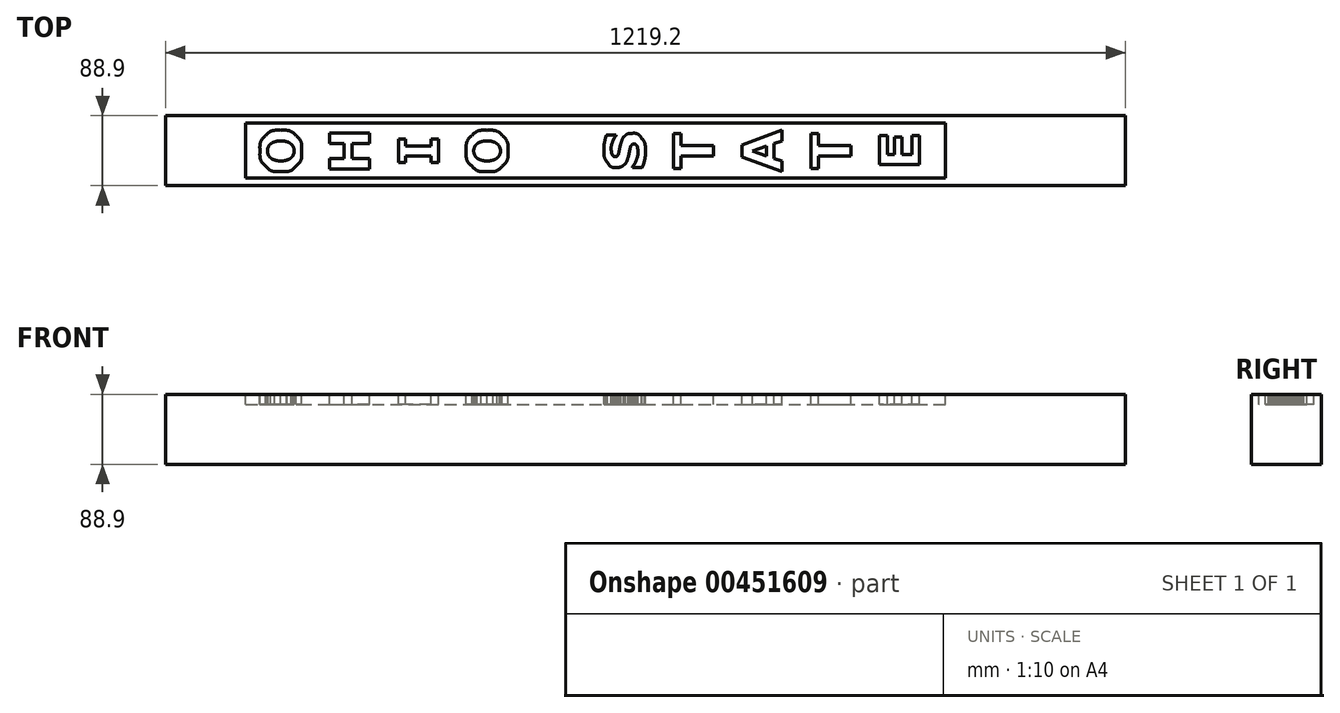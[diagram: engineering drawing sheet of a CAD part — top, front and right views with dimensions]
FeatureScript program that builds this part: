
annotation { "Feature Type Name" : "Feature", "Feature Type Description" : "" }
export const myFeature = defineFeature(function(context is Context, id is Id, definition is map)
    precondition{}
    {
        {
            var Q0;
            Q0=qCreatedBy(makeId("Right.planeOp"),FACE);
            var sketch = newSketch(context, id + "F0", { "sketchPlane" : qUnion([Q0])});
            skLineSegment(sketch, "E0.bottom", {"start": v(0, 0) * mm, "end": v(88.9, 0) * mm});
            skLineSegment(sketch, "E0.top", {"start": v(0, 88.9) * mm, "end": v(88.9, 88.9) * mm});
            skLineSegment(sketch, "E0.left", {"start": v(0, 0) * mm, "end": v(0, 88.9) * mm});
            skLineSegment(sketch, "E0.right", {"start": v(88.9, 0) * mm, "end": v(88.9, 88.9) * mm});
            skSolve(sketch);
        }
        {
            var Q0;
            Q0 = qSketchRegion(id + "F0", true);
            extrude(context, id + "F1", {"entities" : qUnion([Q0]), "depth" : 1219.2 * mm});
        }
        {
            var Q0;
            Q0=makeQuery(id+"F1.opExtrude","SWEPT_FACE",FACE,{"disambiguationData":[OSD([sQuery(id+"F0.wireOp",EDGE,"E0.top")])]});
            var sketch = newSketch(context, id + "F2", { "sketchPlane" : qUnion([Q0])});
            skFitSpline(sketch, "E1", {"points": [v(146.34, 70.3) * mm, v(154.44, 70.3) * mm, v(160.88, 67.98) * mm, v(165.65, 63.34) * mm]});
            skFitSpline(sketch, "E2", {"points": [v(165.65, 63.34) * mm, v(170.4, 58.7) * mm, v(172.78, 52.29) * mm, v(172.78, 44.1) * mm]});
            skFitSpline(sketch, "E3", {"points": [v(172.78, 44.1) * mm, v(172.78, 35.93) * mm, v(170.4, 29.53) * mm, v(165.65, 24.9) * mm]});
            skFitSpline(sketch, "E4", {"points": [v(165.65, 24.9) * mm, v(160.88, 20.25) * mm, v(154.44, 17.93) * mm, v(146.34, 17.93) * mm]});
            skFitSpline(sketch, "E5", {"points": [v(146.34, 17.93) * mm, v(138.18, 17.93) * mm, v(131.73, 20.25) * mm, v(127, 24.9) * mm]});
            skFitSpline(sketch, "E6", {"points": [v(127, 24.9) * mm, v(122.25, 29.53) * mm, v(119.87, 35.93) * mm, v(119.87, 44.1) * mm]});
            skFitSpline(sketch, "E7", {"points": [v(119.87, 44.1) * mm, v(119.87, 52.24) * mm, v(122.25, 58.64) * mm, v(127, 63.3) * mm]});
            skFitSpline(sketch, "E8", {"points": [v(127, 63.3) * mm, v(131.73, 67.97) * mm, v(138.18, 70.3) * mm, v(146.34, 70.3) * mm]});
            skFitSpline(sketch, "E9", {"points": [v(159.2, 52.94) * mm, v(157.66, 54.2) * mm, v(155.84, 55.15) * mm, v(153.75, 55.77) * mm]});
            skFitSpline(sketch, "E10", {"points": [v(153.75, 55.77) * mm, v(151.63, 56.38) * mm, v(149.15, 56.69) * mm, v(146.31, 56.69) * mm]});
            skFitSpline(sketch, "E11", {"points": [v(146.31, 56.69) * mm, v(143.26, 56.69) * mm, v(140.67, 56.34) * mm, v(138.53, 55.63) * mm]});
            skFitSpline(sketch, "E12", {"points": [v(138.53, 55.63) * mm, v(136.4, 54.93) * mm, v(134.66, 54) * mm, v(133.35, 52.87) * mm]});
            skFitSpline(sketch, "E13", {"points": [v(133.35, 52.87) * mm, v(131.98, 51.7) * mm, v(131, 50.37) * mm, v(130.38, 48.84) * mm]});
            skFitSpline(sketch, "E14", {"points": [v(130.38, 48.84) * mm, v(129.76, 47.34) * mm, v(129.46, 45.77) * mm, v(129.46, 44.13) * mm]});
            skFitSpline(sketch, "E15", {"points": [v(129.46, 44.13) * mm, v(129.46, 42.47) * mm, v(129.75, 40.9) * mm, v(130.34, 39.43) * mm]});
            skFitSpline(sketch, "E16", {"points": [v(130.34, 39.43) * mm, v(130.93, 37.97) * mm, v(131.91, 36.63) * mm, v(133.28, 35.4) * mm]});
            skFitSpline(sketch, "E17", {"points": [v(133.28, 35.4) * mm, v(134.55, 34.26) * mm, v(136.31, 33.33) * mm, v(138.57, 32.6) * mm]});
            skFitSpline(sketch, "E18", {"points": [v(138.57, 32.6) * mm, v(140.8, 31.9) * mm, v(143.39, 31.54) * mm, v(146.34, 31.54) * mm]});
            skFitSpline(sketch, "E19", {"points": [v(146.34, 31.54) * mm, v(149.37, 31.54) * mm, v(151.95, 31.89) * mm, v(154.09, 32.57) * mm]});
            skFitSpline(sketch, "E20", {"points": [v(154.09, 32.57) * mm, v(156.2, 33.27) * mm, v(157.93, 34.2) * mm, v(159.27, 35.33) * mm]});
            skFitSpline(sketch, "E21", {"points": [v(159.27, 35.33) * mm, v(160.62, 36.47) * mm, v(161.6, 37.8) * mm, v(162.24, 39.32) * mm]});
            skFitSpline(sketch, "E22", {"points": [v(162.24, 39.32) * mm, v(162.88, 40.85) * mm, v(163.2, 42.45) * mm, v(163.2, 44.13) * mm]});
            skFitSpline(sketch, "E23", {"points": [v(163.2, 44.13) * mm, v(163.2, 45.82) * mm, v(162.88, 47.42) * mm, v(162.24, 48.94) * mm]});
            skFitSpline(sketch, "E24", {"points": [v(162.24, 48.94) * mm, v(161.58, 50.47) * mm, v(160.57, 51.8) * mm, v(159.2, 52.94) * mm]});
            skLineSegment(sketch, "E25", {"start": v(259.07, 66.86) * mm, "end": v(259.07, 53.75) * mm});
            skLineSegment(sketch, "E26", {"start": v(259.07, 53.75) * mm, "end": v(236.69, 53.75) * mm});
            skLineSegment(sketch, "E27", {"start": v(236.69, 53.75) * mm, "end": v(236.69, 34.41) * mm});
            skLineSegment(sketch, "E28", {"start": v(236.69, 34.41) * mm, "end": v(259.07, 34.41) * mm});
            skLineSegment(sketch, "E29", {"start": v(259.07, 34.41) * mm, "end": v(259.07, 21.3) * mm});
            skLineSegment(sketch, "E30", {"start": v(259.07, 21.3) * mm, "end": v(208.27, 21.3) * mm});
            skLineSegment(sketch, "E31", {"start": v(208.27, 21.3) * mm, "end": v(208.27, 34.41) * mm});
            skLineSegment(sketch, "E32", {"start": v(208.27, 34.41) * mm, "end": v(226.86, 34.41) * mm});
            skLineSegment(sketch, "E33", {"start": v(226.86, 34.41) * mm, "end": v(226.86, 53.75) * mm});
            skLineSegment(sketch, "E34", {"start": v(226.86, 53.75) * mm, "end": v(208.27, 53.75) * mm});
            skLineSegment(sketch, "E35", {"start": v(208.27, 53.75) * mm, "end": v(208.27, 66.86) * mm});
            skLineSegment(sketch, "E36", {"start": v(208.27, 66.86) * mm, "end": v(259.07, 66.86) * mm});
            skFitSpline(sketch, "E37", {"points": [v(408.36, 70.3) * mm, v(416.46, 70.3) * mm, v(422.9, 67.98) * mm, v(427.67, 63.34) * mm]});
            skFitSpline(sketch, "E38", {"points": [v(427.67, 63.34) * mm, v(432.43, 58.7) * mm, v(434.8, 52.29) * mm, v(434.8, 44.1) * mm]});
            skFitSpline(sketch, "E39", {"points": [v(434.8, 44.1) * mm, v(434.8, 35.93) * mm, v(432.43, 29.53) * mm, v(427.67, 24.9) * mm]});
            skFitSpline(sketch, "E40", {"points": [v(427.67, 24.9) * mm, v(422.9, 20.25) * mm, v(416.46, 17.93) * mm, v(408.36, 17.93) * mm]});
            skFitSpline(sketch, "E41", {"points": [v(408.36, 17.93) * mm, v(400.2, 17.93) * mm, v(393.75, 20.25) * mm, v(389.02, 24.9) * mm]});
            skFitSpline(sketch, "E42", {"points": [v(389.02, 24.9) * mm, v(384.26, 29.53) * mm, v(381.89, 35.93) * mm, v(381.89, 44.1) * mm]});
            skFitSpline(sketch, "E43", {"points": [v(381.89, 44.1) * mm, v(381.89, 52.24) * mm, v(384.26, 58.64) * mm, v(389.02, 63.3) * mm]});
            skFitSpline(sketch, "E44", {"points": [v(389.02, 63.3) * mm, v(393.75, 67.97) * mm, v(400.2, 70.3) * mm, v(408.36, 70.3) * mm]});
            skLineSegment(sketch, "E45", {"start": v(346.4, 58.94) * mm, "end": v(346.4, 29.2) * mm});
            skLineSegment(sketch, "E46", {"start": v(346.4, 29.2) * mm, "end": v(337.4, 29.2) * mm});
            skLineSegment(sketch, "E47", {"start": v(337.4, 29.2) * mm, "end": v(337.4, 37.52) * mm});
            skLineSegment(sketch, "E48", {"start": v(337.4, 37.52) * mm, "end": v(304.61, 37.52) * mm});
            skLineSegment(sketch, "E49", {"start": v(304.61, 37.52) * mm, "end": v(304.61, 29.2) * mm});
            skLineSegment(sketch, "E50", {"start": v(304.61, 29.2) * mm, "end": v(295.6, 29.2) * mm});
            skLineSegment(sketch, "E51", {"start": v(295.6, 29.2) * mm, "end": v(295.6, 58.94) * mm});
            skLineSegment(sketch, "E52", {"start": v(295.6, 58.94) * mm, "end": v(304.61, 58.94) * mm});
            skLineSegment(sketch, "E53", {"start": v(304.61, 58.94) * mm, "end": v(304.61, 50.62) * mm});
            skLineSegment(sketch, "E54", {"start": v(304.61, 50.62) * mm, "end": v(337.4, 50.62) * mm});
            skLineSegment(sketch, "E55", {"start": v(337.4, 50.62) * mm, "end": v(337.4, 58.94) * mm});
            skLineSegment(sketch, "E56", {"start": v(337.4, 58.94) * mm, "end": v(346.4, 58.94) * mm});
            skFitSpline(sketch, "E57", {"points": [v(421.22, 52.94) * mm, v(419.68, 54.2) * mm, v(417.86, 55.15) * mm, v(415.77, 55.77) * mm]});
            skFitSpline(sketch, "E58", {"points": [v(415.77, 55.77) * mm, v(413.65, 56.38) * mm, v(411.17, 56.69) * mm, v(408.33, 56.69) * mm]});
            skFitSpline(sketch, "E59", {"points": [v(408.33, 56.69) * mm, v(405.28, 56.69) * mm, v(402.69, 56.34) * mm, v(400.55, 55.63) * mm]});
            skFitSpline(sketch, "E60", {"points": [v(400.55, 55.63) * mm, v(398.41, 54.93) * mm, v(396.68, 54) * mm, v(395.36, 52.87) * mm]});
            skFitSpline(sketch, "E61", {"points": [v(395.36, 52.87) * mm, v(394, 51.7) * mm, v(393, 50.37) * mm, v(392.4, 48.84) * mm]});
            skFitSpline(sketch, "E62", {"points": [v(392.4, 48.84) * mm, v(391.78, 47.34) * mm, v(391.47, 45.77) * mm, v(391.47, 44.13) * mm]});
            skFitSpline(sketch, "E63", {"points": [v(391.47, 44.13) * mm, v(391.47, 42.47) * mm, v(391.77, 40.9) * mm, v(392.36, 39.43) * mm]});
            skFitSpline(sketch, "E64", {"points": [v(392.36, 39.43) * mm, v(392.95, 37.97) * mm, v(393.93, 36.63) * mm, v(395.3, 35.4) * mm]});
            skFitSpline(sketch, "E65", {"points": [v(395.3, 35.4) * mm, v(396.57, 34.26) * mm, v(398.33, 33.33) * mm, v(400.58, 32.6) * mm]});
            skFitSpline(sketch, "E66", {"points": [v(400.58, 32.6) * mm, v(402.81, 31.9) * mm, v(405.4, 31.54) * mm, v(408.36, 31.54) * mm]});
            skFitSpline(sketch, "E67", {"points": [v(408.36, 31.54) * mm, v(411.39, 31.54) * mm, v(413.97, 31.89) * mm, v(416.1, 32.57) * mm]});
            skFitSpline(sketch, "E68", {"points": [v(416.1, 32.57) * mm, v(418.22, 33.27) * mm, v(419.95, 34.2) * mm, v(421.3, 35.33) * mm]});
            skFitSpline(sketch, "E69", {"points": [v(421.3, 35.33) * mm, v(422.63, 36.47) * mm, v(423.62, 37.8) * mm, v(424.26, 39.32) * mm]});
            skFitSpline(sketch, "E70", {"points": [v(424.26, 39.32) * mm, v(424.9, 40.85) * mm, v(425.22, 42.45) * mm, v(425.22, 44.13) * mm]});
            skFitSpline(sketch, "E71", {"points": [v(425.22, 44.13) * mm, v(425.22, 45.82) * mm, v(424.9, 47.42) * mm, v(424.26, 48.94) * mm]});
            skFitSpline(sketch, "E72", {"points": [v(424.26, 48.94) * mm, v(423.6, 50.47) * mm, v(422.59, 51.8) * mm, v(421.22, 52.94) * mm]});
            skFitSpline(sketch, "E73", {"points": [v(592.46, 66.41) * mm, v(597.46, 66.41) * mm, v(601.53, 64.29) * mm, v(604.67, 60.03) * mm]});
            skFitSpline(sketch, "E74", {"points": [v(604.67, 60.03) * mm, v(607.79, 55.8) * mm, v(609.34, 50.05) * mm, v(609.34, 42.77) * mm]});
            skFitSpline(sketch, "E75", {"points": [v(609.34, 42.77) * mm, v(609.34, 38.56) * mm, v(608.98, 34.89) * mm, v(608.25, 31.75) * mm]});
            skFitSpline(sketch, "E76", {"points": [v(608.25, 31.75) * mm, v(607.5, 28.63) * mm, v(606.56, 25.71) * mm, v(605.42, 22.98) * mm]});
            skFitSpline(sketch, "E77", {"points": [v(593.24, 24.41) * mm, v(595.4, 27.12) * mm, v(597.06, 30.15) * mm, v(598.22, 33.49) * mm]});
            skFitSpline(sketch, "E78", {"points": [v(598.22, 33.49) * mm, v(599.38, 36.86) * mm, v(599.96, 40.09) * mm, v(599.96, 43.18) * mm]});
            skFitSpline(sketch, "E79", {"points": [v(599.96, 43.18) * mm, v(599.96, 43.97) * mm, v(599.9, 45.02) * mm, v(599.76, 46.32) * mm]});
            skFitSpline(sketch, "E80", {"points": [v(599.76, 46.32) * mm, v(599.62, 47.61) * mm, v(599.4, 48.67) * mm, v(599.08, 49.5) * mm]});
            skFitSpline(sketch, "E81", {"points": [v(599.08, 49.5) * mm, v(598.67, 50.5) * mm, v(598.15, 51.3) * mm, v(597.54, 51.95) * mm]});
            skFitSpline(sketch, "E82", {"points": [v(597.54, 51.95) * mm, v(596.93, 52.6) * mm, v(596.02, 52.94) * mm, v(594.81, 52.94) * mm]});
            skFitSpline(sketch, "E83", {"points": [v(594.81, 52.94) * mm, v(593.7, 52.94) * mm, v(592.74, 52.46) * mm, v(591.94, 51.5) * mm]});
            skFitSpline(sketch, "E84", {"points": [v(591.94, 51.5) * mm, v(591.13, 50.57) * mm, v(590.5, 49.2) * mm, v(590.07, 47.38) * mm]});
            skFitSpline(sketch, "E85", {"points": [v(590.07, 47.38) * mm, v(589.61, 45.46) * mm, v(589.2, 43.44) * mm, v(588.8, 41.3) * mm]});
            skFitSpline(sketch, "E86", {"points": [v(588.8, 41.3) * mm, v(588.4, 39.19) * mm, v(587.88, 37.2) * mm, v(587.27, 35.33) * mm]});
            skFitSpline(sketch, "E87", {"points": [v(587.27, 35.33) * mm, v(585.88, 31.06) * mm, v(584, 27.97) * mm, v(581.64, 26.09) * mm]});
            skFitSpline(sketch, "E88", {"points": [v(581.64, 26.09) * mm, v(579.25, 24.22) * mm, v(576.3, 23.29) * mm, v(572.77, 23.29) * mm]});
            skFitSpline(sketch, "E89", {"points": [v(572.77, 23.29) * mm, v(568.04, 23.29) * mm, v(564.19, 25.4) * mm, v(561.2, 29.63) * mm]});
            skFitSpline(sketch, "E90", {"points": [v(561.2, 29.63) * mm, v(558.2, 33.89) * mm, v(556.7, 39.35) * mm, v(556.7, 46.01) * mm]});
            skFitSpline(sketch, "E91", {"points": [v(556.7, 46.01) * mm, v(556.7, 49.35) * mm, v(557.03, 52.65) * mm, v(557.7, 55.9) * mm]});
            skFitSpline(sketch, "E92", {"points": [v(557.7, 55.9) * mm, v(558.33, 59.18) * mm, v(559.14, 62.01) * mm, v(560.11, 64.4) * mm]});
            skLineSegment(sketch, "E93", {"start": v(605.42, 22.98) * mm, "end": v(593.24, 22.98) * mm});
            skLineSegment(sketch, "E94", {"start": v(593.24, 22.98) * mm, "end": v(593.24, 24.41) * mm});
            skLineSegment(sketch, "E95", {"start": v(593.24, 24.41) * mm, "end": v(605.42, 22.98) * mm});
            skFitSpline(sketch, "E96", {"points": [v(571.82, 63) * mm, v(570.18, 60.95) * mm, v(568.81, 58.44) * mm, v(567.72, 55.46) * mm]});
            skFitSpline(sketch, "E97", {"points": [v(567.72, 55.46) * mm, v(566.6, 52.5) * mm, v(566.05, 49.48) * mm, v(566.05, 46.39) * mm]});
            skFitSpline(sketch, "E98", {"points": [v(566.05, 46.39) * mm, v(566.05, 45.3) * mm, v(566.13, 44.2) * mm, v(566.29, 43.11) * mm]});
            skFitSpline(sketch, "E99", {"points": [v(566.29, 43.11) * mm, v(566.43, 42.04) * mm, v(566.7, 41) * mm, v(567.1, 40) * mm]});
            skFitSpline(sketch, "E100", {"points": [v(567.1, 40) * mm, v(567.45, 39.12) * mm, v(567.97, 38.36) * mm, v(568.68, 37.72) * mm]});
            skFitSpline(sketch, "E101", {"points": [v(568.68, 37.72) * mm, v(569.36, 37.08) * mm, v(570.14, 36.76) * mm, v(571.03, 36.76) * mm]});
            skFitSpline(sketch, "E102", {"points": [v(571.03, 36.76) * mm, v(572.37, 36.76) * mm, v(573.4, 37.28) * mm, v(574.14, 38.3) * mm]});
            skFitSpline(sketch, "E103", {"points": [v(574.14, 38.3) * mm, v(574.84, 39.32) * mm, v(575.49, 41.26) * mm, v(576.08, 44.1) * mm]});
            skFitSpline(sketch, "E104", {"points": [v(576.08, 44.1) * mm, v(576.47, 45.96) * mm, v(576.84, 47.75) * mm, v(577.2, 49.46) * mm]});
            skFitSpline(sketch, "E105", {"points": [v(577.2, 49.46) * mm, v(577.57, 51.18) * mm, v(578.07, 53.04) * mm, v(578.7, 55.02) * mm]});
            skFitSpline(sketch, "E106", {"points": [v(578.7, 55.02) * mm, v(579.98, 58.9) * mm, v(581.72, 61.77) * mm, v(583.93, 63.61) * mm]});
            skFitSpline(sketch, "E107", {"points": [v(583.93, 63.61) * mm, v(586.11, 65.48) * mm, v(588.95, 66.41) * mm, v(592.46, 66.41) * mm]});
            skLineSegment(sketch, "E108", {"start": v(560.11, 64.4) * mm, "end": v(571.82, 64.4) * mm});
            skLineSegment(sketch, "E109", {"start": v(571.82, 64.4) * mm, "end": v(571.82, 63) * mm});
            skLineSegment(sketch, "E110", {"start": v(571.82, 63) * mm, "end": v(560.11, 64.4) * mm});
            skLineSegment(sketch, "E111", {"start": v(654.79, 66.51) * mm, "end": v(654.79, 50.65) * mm});
            skLineSegment(sketch, "E112", {"start": v(654.79, 50.65) * mm, "end": v(695.76, 50.65) * mm});
            skLineSegment(sketch, "E113", {"start": v(695.76, 50.65) * mm, "end": v(695.76, 37.55) * mm});
            skLineSegment(sketch, "E114", {"start": v(695.76, 37.55) * mm, "end": v(654.79, 37.55) * mm});
            skLineSegment(sketch, "E115", {"start": v(654.79, 37.55) * mm, "end": v(654.79, 21.69) * mm});
            skLineSegment(sketch, "E116", {"start": v(654.79, 21.69) * mm, "end": v(644.96, 21.69) * mm});
            skLineSegment(sketch, "E117", {"start": v(644.96, 21.69) * mm, "end": v(644.96, 66.51) * mm});
            skLineSegment(sketch, "E118", {"start": v(644.96, 66.51) * mm, "end": v(654.79, 66.51) * mm});
            skLineSegment(sketch, "E119", {"start": v(783.1, 70.37) * mm, "end": v(783.1, 56.83) * mm});
            skLineSegment(sketch, "E120", {"start": v(783.1, 56.83) * mm, "end": v(772.83, 53.31) * mm});
            skLineSegment(sketch, "E121", {"start": v(772.83, 53.31) * mm, "end": v(772.83, 34.48) * mm});
            skLineSegment(sketch, "E122", {"start": v(772.83, 34.48) * mm, "end": v(783.1, 30.96) * mm});
            skLineSegment(sketch, "E123", {"start": v(783.1, 30.96) * mm, "end": v(783.1, 17.76) * mm});
            skLineSegment(sketch, "E124", {"start": v(783.1, 17.76) * mm, "end": v(732.3, 36.53) * mm});
            skLineSegment(sketch, "E125", {"start": v(732.3, 36.53) * mm, "end": v(732.3, 51.6) * mm});
            skLineSegment(sketch, "E126", {"start": v(732.3, 51.6) * mm, "end": v(783.1, 70.37) * mm});
            skLineSegment(sketch, "E127", {"start": v(763.52, 50.14) * mm, "end": v(745.3, 43.9) * mm});
            skLineSegment(sketch, "E128", {"start": v(745.3, 43.9) * mm, "end": v(763.52, 37.65) * mm});
            skLineSegment(sketch, "E129", {"start": v(763.52, 37.65) * mm, "end": v(763.52, 50.14) * mm});
            skLineSegment(sketch, "E130", {"start": v(829.47, 66.51) * mm, "end": v(829.47, 50.65) * mm});
            skLineSegment(sketch, "E131", {"start": v(829.47, 50.65) * mm, "end": v(870.44, 50.65) * mm});
            skLineSegment(sketch, "E132", {"start": v(870.44, 50.65) * mm, "end": v(870.44, 37.55) * mm});
            skLineSegment(sketch, "E133", {"start": v(870.44, 37.55) * mm, "end": v(829.47, 37.55) * mm});
            skLineSegment(sketch, "E134", {"start": v(829.47, 37.55) * mm, "end": v(829.47, 21.69) * mm});
            skLineSegment(sketch, "E135", {"start": v(829.47, 21.69) * mm, "end": v(819.64, 21.69) * mm});
            skLineSegment(sketch, "E136", {"start": v(819.64, 21.69) * mm, "end": v(819.64, 66.51) * mm});
            skLineSegment(sketch, "E137", {"start": v(819.64, 66.51) * mm, "end": v(829.47, 66.51) * mm});
            skLineSegment(sketch, "E138", {"start": v(957.78, 63.44) * mm, "end": v(957.78, 26.7) * mm});
            skLineSegment(sketch, "E139", {"start": v(957.78, 26.7) * mm, "end": v(906.98, 26.7) * mm});
            skLineSegment(sketch, "E140", {"start": v(906.98, 26.7) * mm, "end": v(906.98, 63.44) * mm});
            skLineSegment(sketch, "E141", {"start": v(906.98, 63.44) * mm, "end": v(916.8, 63.44) * mm});
            skLineSegment(sketch, "E142", {"start": v(916.8, 63.44) * mm, "end": v(916.8, 39.73) * mm});
            skLineSegment(sketch, "E143", {"start": v(916.8, 39.73) * mm, "end": v(925.57, 39.73) * mm});
            skLineSegment(sketch, "E144", {"start": v(925.57, 39.73) * mm, "end": v(925.57, 61.74) * mm});
            skLineSegment(sketch, "E145", {"start": v(925.57, 61.74) * mm, "end": v(935.4, 61.74) * mm});
            skLineSegment(sketch, "E146", {"start": v(935.4, 61.74) * mm, "end": v(935.4, 39.73) * mm});
            skLineSegment(sketch, "E147", {"start": v(935.4, 39.73) * mm, "end": v(947.95, 39.73) * mm});
            skLineSegment(sketch, "E148", {"start": v(947.95, 39.73) * mm, "end": v(947.95, 63.44) * mm});
            skLineSegment(sketch, "E149", {"start": v(947.95, 63.44) * mm, "end": v(957.78, 63.44) * mm});
            skLineSegment(sketch, "E150.bottom", {"start": v(101.6, 79.37) * mm, "end": v(990.6, 79.37) * mm});
            skLineSegment(sketch, "E150.top", {"start": v(101.6, 9.53) * mm, "end": v(990.6, 9.53) * mm});
            skLineSegment(sketch, "E150.left", {"start": v(101.6, 79.37) * mm, "end": v(101.6, 9.53) * mm});
            skLineSegment(sketch, "E150.right", {"start": v(990.6, 79.37) * mm, "end": v(990.6, 9.53) * mm});
            skSolve(sketch);
        }
        {
            var Q0;
            Q0 = qSketchRegion(id + "F2", true);
            var Q1;
            Q1=makeQuery(id+"F2.imprint","IMPRINT",FACE,{"disambiguationData":[TD([[makeQuery(id+"F2.imprint","IMPRINT",EDGE,{"derivedFrom":sQuery(id+"F2.wireOp",EDGE,"E9")}),1.0]])]});
            var Q2;
            Q2=makeQuery(id+"F2.imprint","IMPRINT",FACE,{"disambiguationData":[TD([[makeQuery(id+"F2.imprint","IMPRINT",EDGE,{"derivedFrom":sQuery(id+"F2.wireOp",EDGE,"E57")}),1.0]])]});
            var Q3;
            Q3=makeQuery(id+"F2.imprint","IMPRINT",FACE,{"disambiguationData":[TD([[makeQuery(id+"F2.imprint","IMPRINT",EDGE,{"derivedFrom":sQuery(id+"F2.wireOp",EDGE,"E127")}),1.0]])]});
            extrude(context, id + "F3", {"entities" : qUnion([Q0, Q1, Q2, Q3]), "operationType" : NewBodyOperationType.REMOVE, "oppositeDirection" : true, "depth" : 12.7 * mm});
        }
    });
